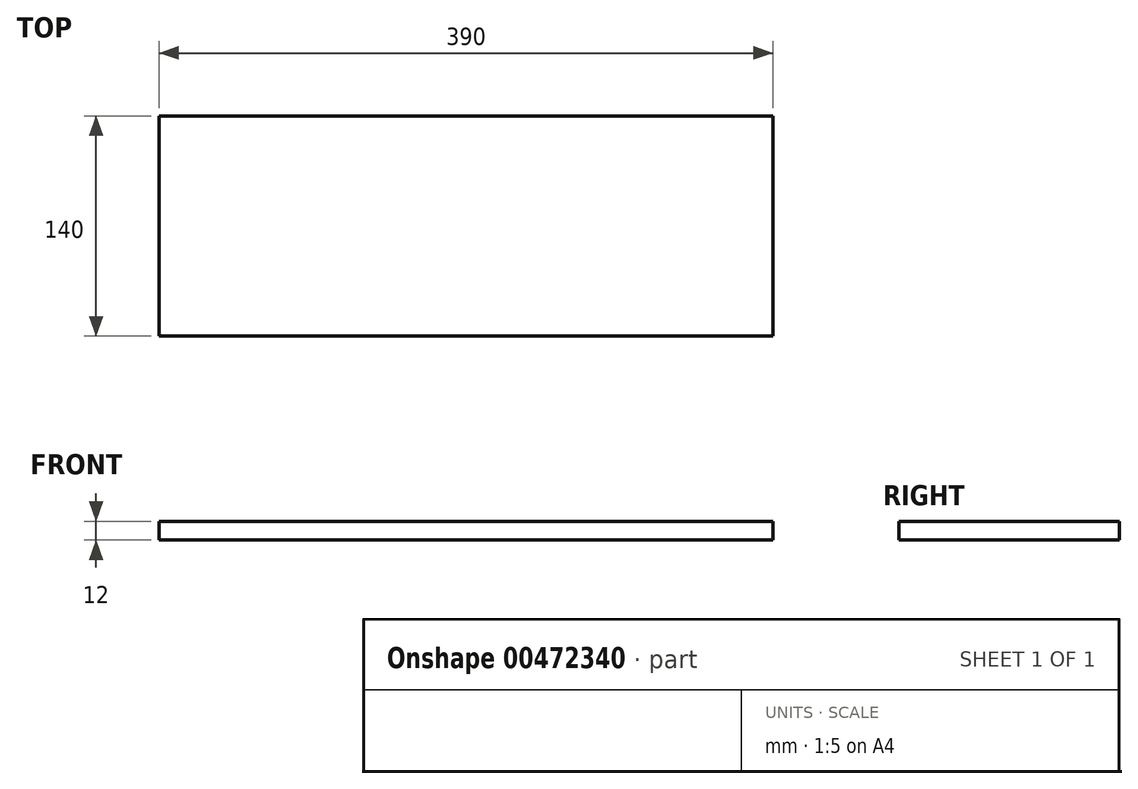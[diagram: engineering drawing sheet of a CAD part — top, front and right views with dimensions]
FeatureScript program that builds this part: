
annotation { "Feature Type Name" : "Feature", "Feature Type Description" : "" }
export const myFeature = defineFeature(function(context is Context, id is Id, definition is map)
    precondition{}
    {
        {
            var Q0;
            Q0=qCreatedBy(makeId("Right.planeOp"),FACE);
            var sketch = newSketch(context, id + "F0", { "sketchPlane" : qUnion([Q0])});
            skLineSegment(sketch, "E0.bottom", {"start": v(70, 6) * mm, "end": v(-70, 6) * mm});
            skLineSegment(sketch, "E0.top", {"start": v(70, -6) * mm, "end": v(-70, -6) * mm});
            skLineSegment(sketch, "E0.left", {"start": v(70, 6) * mm, "end": v(70, -6) * mm});
            skLineSegment(sketch, "E0.right", {"start": v(-70, 6) * mm, "end": v(-70, -6) * mm});
            skPoint(sketch, "E0.middle", {"position": v(0, 0) * mm});
            skSolve(sketch);
        }
        {
            var Q0;
            Q0=makeQuery(id+"F0.imprint","IMPRINT",FACE,{"disambiguationData":[TD([[makeQuery(id+"F0.imprint","IMPRINT",EDGE,{"derivedFrom":sQuery(id+"F0.wireOp",EDGE,"E0.bottom")}),1.0]])]});
            extrude(context, id + "F1", {"entities" : qUnion([Q0]), "endBound" : BoundingType.SYMMETRIC, "depth" : 390 * mm});
        }
    });
